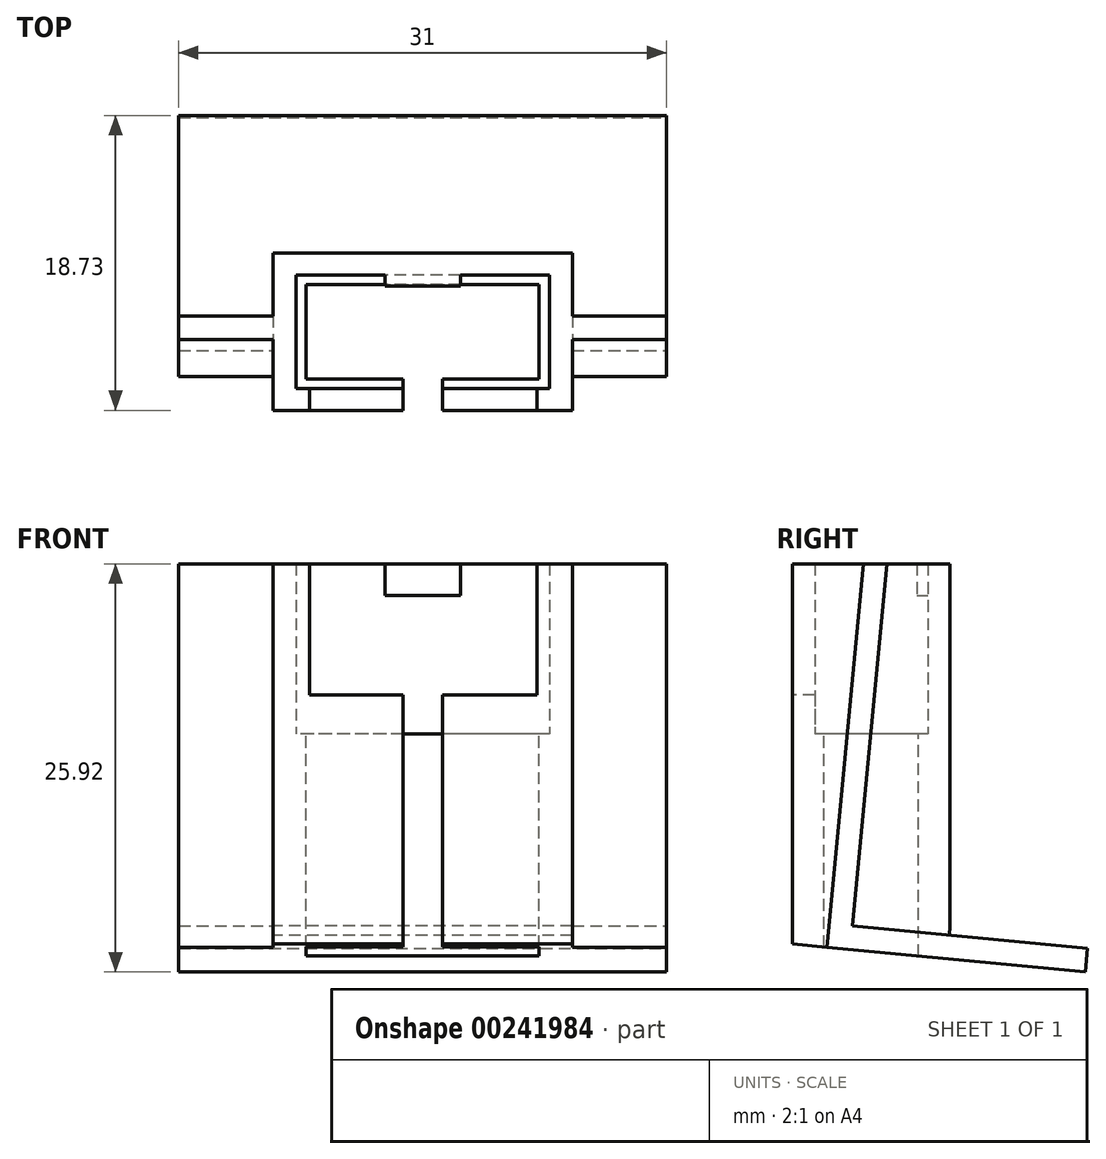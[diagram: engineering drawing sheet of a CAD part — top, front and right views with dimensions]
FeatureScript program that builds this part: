
annotation { "Feature Type Name" : "Feature", "Feature Type Description" : "" }
export const myFeature = defineFeature(function(context is Context, id is Id, definition is map)
    precondition{}
    {
        {
            var Q0;
            Q0=qCreatedBy(makeId("Top.planeOp"),FACE);
            var sketch = newSketch(context, id + "F0", { "sketchPlane" : qUnion([Q0])});
            skLineSegment(sketch, "E0.bottom", {"start": v(8.05, 3.6) * mm, "end": v(-8.05, 3.6) * mm});
            skLineSegment(sketch, "E0.top", {"start": v(8.05, -3.6) * mm, "end": v(-8.05, -3.6) * mm});
            skLineSegment(sketch, "E0.left", {"start": v(8.05, 3.6) * mm, "end": v(8.05, -3.6) * mm});
            skLineSegment(sketch, "E0.right", {"start": v(-8.05, 3.6) * mm, "end": v(-8.05, -3.6) * mm});
            skPoint(sketch, "E0.middle", {"position": v(0, 0) * mm});
            skLineSegment(sketch, "E1.bottom", {"start": v(9.5, 5) * mm, "end": v(-9.5, 5) * mm});
            skLineSegment(sketch, "E1.top", {"start": v(9.5, -5) * mm, "end": v(-9.5, -5) * mm});
            skLineSegment(sketch, "E1.left", {"start": v(9.5, 5) * mm, "end": v(9.5, -5) * mm});
            skLineSegment(sketch, "E1.right", {"start": v(-9.5, 5) * mm, "end": v(-9.5, -5) * mm});
            skLineSegment(sketch, "E2.bottom", {"start": v(7.4, 3) * mm, "end": v(-7.4, 3) * mm});
            skLineSegment(sketch, "E2.top", {"start": v(7.4, -3) * mm, "end": v(-7.4, -3) * mm});
            skLineSegment(sketch, "E2.left", {"start": v(7.4, 3) * mm, "end": v(7.4, -3) * mm});
            skLineSegment(sketch, "E2.right", {"start": v(-7.4, 3) * mm, "end": v(-7.4, -3) * mm});
            skSolve(sketch);
        }
        {
            var Q0;
            Q0=makeQuery(id+"F0.imprint","IMPRINT",FACE,{"disambiguationData":[TD([[makeQuery(id+"F0.imprint","IMPRINT",EDGE,{"derivedFrom":sQuery(id+"F0.wireOp",EDGE,"E0.bottom")}),-1.0]])]});
            extrude(context, id + "F1", {"entities" : qUnion([Q0]), "depth" : 10.8 * mm});
        }
        {
            var Q0;
            Q0=makeQuery(id+"F0.imprint","IMPRINT",FACE,{"disambiguationData":[TD([[makeQuery(id+"F0.imprint","IMPRINT",EDGE,{"derivedFrom":sQuery(id+"F0.wireOp",EDGE,"E0.bottom")}),1.0]])]});
            var Q1;
            Q1=makeQuery(id+"F0.imprint","IMPRINT",FACE,{"disambiguationData":[TD([[makeQuery(id+"F0.imprint","IMPRINT",EDGE,{"derivedFrom":sQuery(id+"F0.wireOp",EDGE,"E0.bottom")}),-1.0]])]});
            extrude(context, id + "F2", {"entities" : qUnion([Q0, Q1]), "operationType" : NewBodyOperationType.ADD, "oppositeDirection" : true, "depth" : 12.2 * mm});
        }
        {
            var Q0;
            {var subQ0=sQuery(id+"F0.wireOp",EDGE,"E1.right");Q0=makeQuery(id+"F2.boolean.opBoolean","MERGE",FACE,{"derivedFrom":[makeQuery(id+"F1.opExtrude","SWEPT_FACE",FACE,{"disambiguationData":[OSD([subQ0])]}),makeQuery(id+"F2.opExtrude","SWEPT_FACE",FACE,{"disambiguationData":[OSD([subQ0])]})]});}
            var sketch = newSketch(context, id + "F3", { "sketchPlane" : qUnion([Q0])});
            skLineSegment(sketch, "E3", {"start": v(-1, 10.8) * mm, "end": v(1.2, -12.2) * mm});
            skLineSegment(sketch, "E4", {"start": v(1.2, -12.2) * mm, "end": v(-13.73, -13.63) * mm});
            skLineSegment(sketch, "E5.0", {"start": v(2.84, -13.55) * mm, "end": v(-13.59, -15.12) * mm});
            skLineSegment(sketch, "E5.1", {"start": v(0.5, 10.94) * mm, "end": v(2.84, -13.55) * mm});
            skLineSegment(sketch, "E6", {"start": v(-13.73, -13.63) * mm, "end": v(-13.59, -15.12) * mm});
            skLineSegment(sketch, "E7", {"start": v(-1, 10.8) * mm, "end": v(0.5, 10.8) * mm});
            skLineSegment(sketch, "E8", {"start": v(-5, -12.2) * mm, "end": v(-4.94, -12.79) * mm});
            skLineSegment(sketch, "E9", {"start": v(-4.94, -12.79) * mm, "end": v(1.2, -12.2) * mm});
            skLineSegment(sketch, "E10", {"start": v(2.84, -13.55) * mm, "end": v(5, -13.34) * mm});
            skLineSegment(sketch, "E11", {"start": v(5, -13.34) * mm, "end": v(5, -12.2) * mm});
            skLineSegment(sketch, "E12", {"start": v(5, -12.2) * mm, "end": v(2.7, -12.2) * mm});
            skLineSegment(sketch, "E13", {"start": v(2.7, -12.2) * mm, "end": v(2.84, -13.55) * mm});
            skSolve(sketch);
        }
        {
            var Q0;
            {var subQ7=sQuery(id+"F3.wireOp",EDGE,"E3");Q0=makeQuery(id+"F3.imprint","IMPRINT",FACE,{"disambiguationData":[TD([[makeQuery(id+"F3.imprint","IMPRINT",EDGE,{"derivedFrom":subQ7}),1.0]])]});}
            var Q1;
            Q1=makeQuery(id+"F3.imprint","IMPRINT",FACE,{"disambiguationData":[TD([[makeQuery(id+"F3.imprint","IMPRINT",EDGE,{"derivedFrom":sQuery(id+"F3.wireOp",EDGE,"E4")}),1.0]])]});
            extrude(context, id + "F4", {"entities" : qUnion([Q0, Q1]), "operationType" : NewBodyOperationType.ADD, "depth" : 6 * mm, "hasSecondDirection" : true, "secondDirectionOppositeDirection" : true, "secondDirectionDepth" : 25 * mm});
        }
        {
            var Q0;
            {var subQ0=sQuery(id+"F3.wireOp",EDGE,"E8");Q0=makeQuery(id+"F3.imprint","IMPRINT",FACE,{"disambiguationData":[TD([[makeQuery(id+"F3.imprint","IMPRINT",EDGE,{"derivedFrom":subQ0}),1.0]])]});}
            var Q1;
            Q1=makeQuery(id+"F3.imprint","IMPRINT",FACE,{"disambiguationData":[TD([[makeQuery(id+"F3.imprint","IMPRINT",EDGE,{"derivedFrom":sQuery(id+"F3.wireOp",EDGE,"E10")}),1.0]])]});
            extrude(context, id + "F5", {"entities" : qUnion([Q0, Q1]), "operationType" : NewBodyOperationType.ADD, "oppositeDirection" : true, "depth" : 19 * mm});
        }
        {
            var Q0;
            Q0=makeQuery(id+"F0.imprint","IMPRINT",FACE,{"disambiguationData":[TD([[makeQuery(id+"F0.imprint","IMPRINT",EDGE,{"derivedFrom":sQuery(id+"F0.wireOp",EDGE,"E2.bottom")}),1.0]])]});
            extrude(context, id + "F6", {"entities" : qUnion([Q0]), "operationType" : NewBodyOperationType.REMOVE, "endBound" : BoundingType.THROUGH_ALL, "oppositeDirection" : true, "depth" : 25 * mm});
        }
        {
            var Q0;
            Q0=makeQuery(id+"F0.imprint","IMPRINT",FACE,{"disambiguationData":[TD([[makeQuery(id+"F0.imprint","IMPRINT",EDGE,{"derivedFrom":sQuery(id+"F0.wireOp",EDGE,"E2.bottom")}),1.0]])]});
            var Q1;
            Q1=makeQuery(id+"F0.imprint","IMPRINT",FACE,{"disambiguationData":[TD([[makeQuery(id+"F0.imprint","IMPRINT",EDGE,{"derivedFrom":sQuery(id+"F0.wireOp",EDGE,"E0.bottom")}),1.0]])]});
            extrude(context, id + "F7", {"entities" : qUnion([Q0, Q1]), "operationType" : NewBodyOperationType.REMOVE, "depth" : 25 * mm});
        }
        {
            var Q0;
            Q0=makeQuery(id+"F1.opExtrude","SWEPT_FACE",FACE,{"disambiguationData":[OSD([sQuery(id+"F0.wireOp",EDGE,"E0.top")])]});
            var sketch = newSketch(context, id + "F8", { "sketchPlane" : qUnion([Q0])});
            skLineSegment(sketch, "E14.bottom", {"start": v(7.17, 10.8) * mm, "end": v(-7.25, 10.8) * mm});
            skLineSegment(sketch, "E14.top", {"start": v(7.17, 2.5) * mm, "end": v(-7.25, 2.5) * mm});
            skLineSegment(sketch, "E14.left", {"start": v(7.17, 10.8) * mm, "end": v(7.17, 2.5) * mm});
            skLineSegment(sketch, "E14.right", {"start": v(-7.25, 10.8) * mm, "end": v(-7.25, 2.5) * mm});
            skSolve(sketch);
        }
        {
            var Q0;
            Q0=makeQuery(id+"F8.imprint","IMPRINT",FACE,{"disambiguationData":[TD([[makeQuery(id+"F8.imprint","IMPRINT",EDGE,{"derivedFrom":sQuery(id+"F8.wireOp",EDGE,"E14.bottom")}),-1.0]])]});
            extrude(context, id + "F9", {"entities" : qUnion([Q0]), "operationType" : NewBodyOperationType.REMOVE, "oppositeDirection" : true, "depth" : 25 * mm});
        }
        {
            var Q0;
            Q0=makeQuery(id+"F1.opExtrude","SWEPT_FACE",FACE,{"disambiguationData":[OSD([sQuery(id+"F0.wireOp",EDGE,"E0.bottom")])]});
            var sketch = newSketch(context, id + "F10", { "sketchPlane" : qUnion([Q0])});
            skLineSegment(sketch, "E15.top", {"start": v(2.4, 8.8) * mm, "end": v(-2.4, 8.8) * mm});
            skLineSegment(sketch, "E15.left", {"start": v(2.4, 10.8) * mm, "end": v(2.4, 8.8) * mm});
            skLineSegment(sketch, "E15.right", {"start": v(-2.4, 10.8) * mm, "end": v(-2.4, 8.8) * mm});
            skPoint(sketch, "E15.middle", {"position": v(0, 10.8) * mm});
            skLineSegment(sketch, "E16", {"start": v(-2.4, 10.8) * mm, "end": v(2.4, 10.8) * mm});
            skPoint(sketch, "E15.bottom.end.orphan", {"position": v(-2.4, 12.8) * mm});
            skPoint(sketch, "E17.orphan", {"position": v(2.4, 12.8) * mm});
            skSolve(sketch);
        }
        {
            var Q0;
            Q0=makeQuery(id+"F10.imprint","IMPRINT",FACE,{"disambiguationData":[TD([[makeQuery(id+"F10.imprint","IMPRINT",EDGE,{"derivedFrom":sQuery(id+"F10.wireOp",EDGE,"E15.top")}),-1.0]])]});
            extrude(context, id + "F11", {"entities" : qUnion([Q0]), "operationType" : NewBodyOperationType.ADD, "depth" : 0.7 * mm});
        }
        {
            var Q0;
            Q0=qCreatedBy(makeId("Top.planeOp"),FACE);
            var sketch = newSketch(context, id + "F12", { "sketchPlane" : qUnion([Q0])});
            skLineSegment(sketch, "E18.bottom", {"start": v(1.25, -2.5) * mm, "end": v(-1.25, -2.5) * mm});
            skLineSegment(sketch, "E18.top", {"start": v(1.25, -7.5) * mm, "end": v(-1.25, -7.5) * mm});
            skLineSegment(sketch, "E18.left", {"start": v(1.25, -2.5) * mm, "end": v(1.25, -7.5) * mm});
            skLineSegment(sketch, "E18.right", {"start": v(-1.25, -2.5) * mm, "end": v(-1.25, -7.5) * mm});
            skPoint(sketch, "E18.middle", {"position": v(0, -5) * mm});
            skSolve(sketch);
        }
        {
            var Q0;
            Q0=makeQuery(id+"F12.imprint","IMPRINT",FACE,{"disambiguationData":[TD([[makeQuery(id+"F12.imprint","IMPRINT",EDGE,{"derivedFrom":sQuery(id+"F12.wireOp",EDGE,"E18.bottom")}),1.0]])]});
            extrude(context, id + "F13", {"entities" : qUnion([Q0]), "operationType" : NewBodyOperationType.REMOVE, "oppositeDirection" : true, "depth" : 25 * mm, "hasSecondDirection" : true, "secondDirectionOppositeDirection" : false, "secondDirectionDepth" : 25 * mm});
        }
    });
